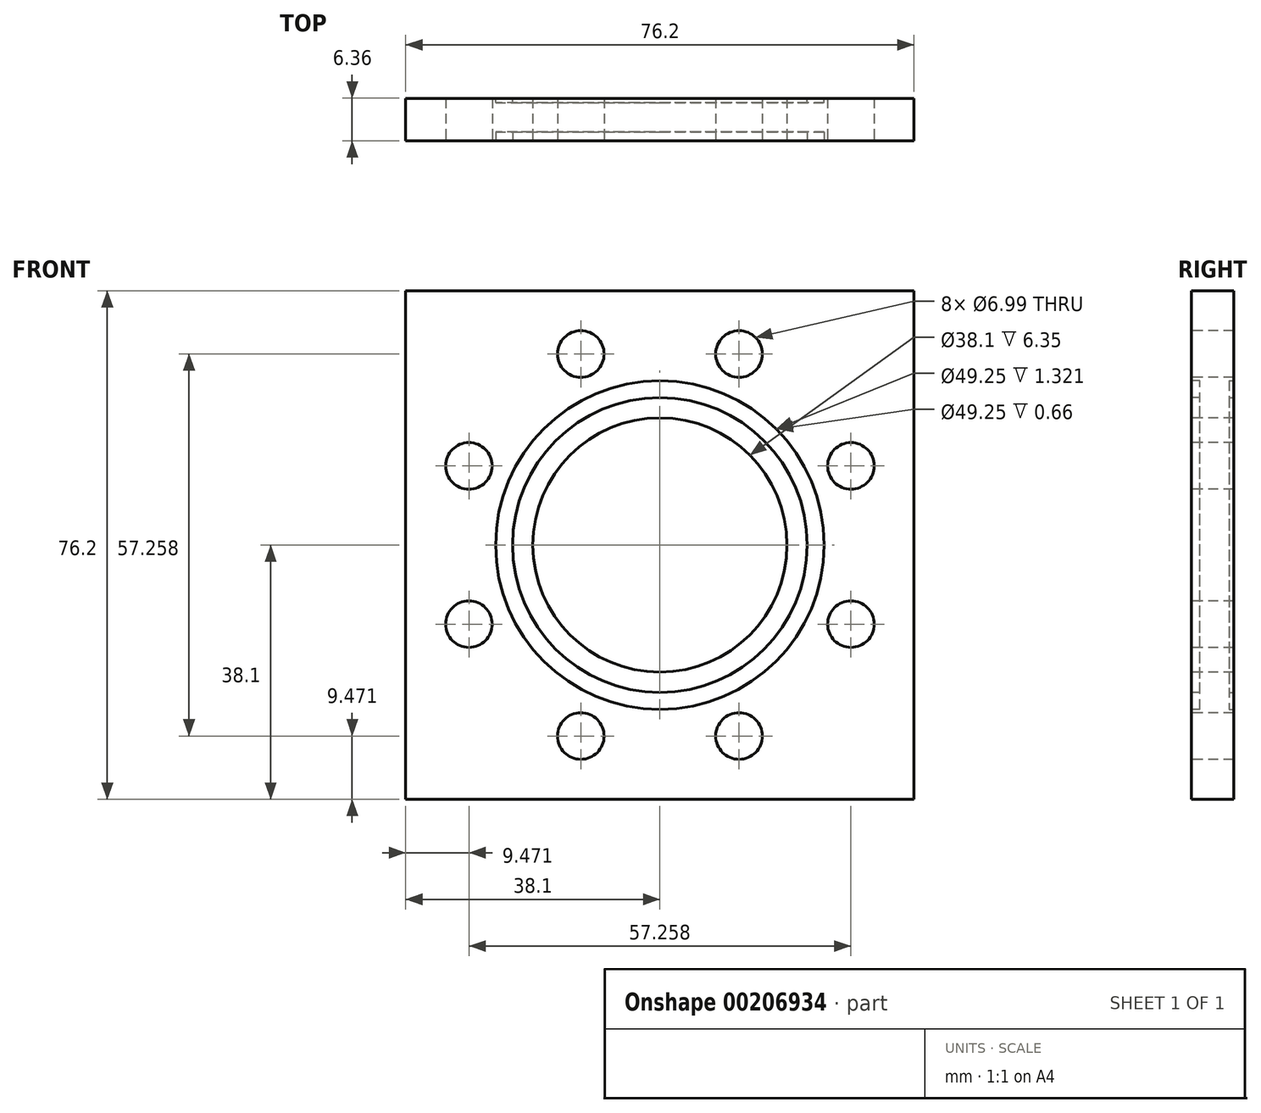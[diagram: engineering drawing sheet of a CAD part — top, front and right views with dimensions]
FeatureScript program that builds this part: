
annotation { "Feature Type Name" : "Feature", "Feature Type Description" : "" }
export const myFeature = defineFeature(function(context is Context, id is Id, definition is map)
    precondition{}
    {
        {
            var Q0;
            Q0=qCreatedBy(makeId("Front.planeOp"),FACE);
            var sketch = newSketch(context, id + "F0", { "sketchPlane" : qUnion([Q0])});
            skLineSegment(sketch, "E0.bottom", {"start": v(-38.1, 38.1) * mm, "end": v(38.1, 38.1) * mm});
            skLineSegment(sketch, "E0.top", {"start": v(-38.1, -38.1) * mm, "end": v(38.1, -38.1) * mm});
            skLineSegment(sketch, "E0.left", {"start": v(-38.1, 38.1) * mm, "end": v(-38.1, -38.1) * mm});
            skLineSegment(sketch, "E0.right", {"start": v(38.1, 38.1) * mm, "end": v(38.1, -38.1) * mm});
            skSolve(sketch);
        }
        {
            var Q0;
            Q0=qSketchRegion(id+"F0",true);
            extrude(context, id + "F1", {"entities" : qUnion([Q0]), "endBound" : BoundingType.SYMMETRIC, "depth" : 6.35 * mm});
        }
        {
            var Q0;
            Q0=makeQuery(id+"F1.opExtrude","CAP_FACE",FACE,{"disambiguationData":[OSD([sQuery(id+"F0.wireOp",EDGE,"E0.bottom"),sQuery(id+"F0.wireOp",EDGE,"E0.top"),sQuery(id+"F0.wireOp",EDGE,"E0.left"),sQuery(id+"F0.wireOp",EDGE,"E0.right")])],"isStart":false});
            var sketch = newSketch(context, id + "F2", { "sketchPlane" : qUnion([Q0])});
            skLineSegment(sketch, "E1", {"start": v(0, 0) * mm, "end": v(11.86, 28.63) * mm, "construction": true});
            skCircle(sketch, "E2", {"center": v(11.86, 28.63) * mm, "radius": 3.5 * mm});
            skCircle(sketch, "E3.1.0", {"center": v(-11.86, 28.63) * mm, "radius": 3.5 * mm});
            skCircle(sketch, "E3.2.0", {"center": v(-28.63, 11.86) * mm, "radius": 3.5 * mm});
            skCircle(sketch, "E3.3.0", {"center": v(-28.63, -11.86) * mm, "radius": 3.5 * mm});
            skCircle(sketch, "E3.4.0", {"center": v(-11.86, -28.63) * mm, "radius": 3.5 * mm});
            skCircle(sketch, "E3.5.0", {"center": v(11.86, -28.63) * mm, "radius": 3.5 * mm});
            skCircle(sketch, "E3.6.0", {"center": v(28.63, -11.86) * mm, "radius": 3.5 * mm});
            skCircle(sketch, "E3.7.0", {"center": v(28.63, 11.86) * mm, "radius": 3.5 * mm});
            skPoint(sketch, "E3.center", {"position": v(0, 0) * mm});
            skSolve(sketch);
        }
        {
            var Q0;
            Q0=qSketchRegion(id+"F2",true);
            extrude(context, id + "F3", {"entities" : qUnion([Q0]), "operationType" : NewBodyOperationType.REMOVE, "oppositeDirection" : true, "depth" : 25.4 * mm});
        }
        {
            var Q0;
            Q0=makeQuery(id+"F1.opExtrude","CAP_FACE",FACE,{"disambiguationData":[OSD([sQuery(id+"F0.wireOp",EDGE,"E0.bottom"),sQuery(id+"F0.wireOp",EDGE,"E0.top"),sQuery(id+"F0.wireOp",EDGE,"E0.left"),sQuery(id+"F0.wireOp",EDGE,"E0.right")])],"isStart":false});
            var sketch = newSketch(context, id + "F4", { "sketchPlane" : qUnion([Q0])});
            skCircle(sketch, "E4", {"center": v(0, 0) * mm, "radius": 19.05 * mm});
            skSolve(sketch);
        }
        {
            var Q0;
            Q0=qSketchRegion(id+"F4",true);
            extrude(context, id + "F5", {"entities" : qUnion([Q0]), "operationType" : NewBodyOperationType.REMOVE, "oppositeDirection" : true, "depth" : 25.4 * mm});
        }
        {
            var Q0;
            Q0=makeQuery(id+"F1.opExtrude","CAP_FACE",FACE,{"disambiguationData":[OSD([sQuery(id+"F0.wireOp",EDGE,"E0.bottom"),sQuery(id+"F0.wireOp",EDGE,"E0.top"),sQuery(id+"F0.wireOp",EDGE,"E0.left"),sQuery(id+"F0.wireOp",EDGE,"E0.right")])],"isStart":false});
            var sketch = newSketch(context, id + "F6", { "sketchPlane" : qUnion([Q0])});
            skCircle(sketch, "E5", {"center": v(0, 0) * mm, "radius": 22.09 * mm});
            skCircle(sketch, "E6", {"center": v(0, 0) * mm, "radius": 24.63 * mm});
            skSolve(sketch);
        }
        {
            var Q0;
            Q0 = qSketchRegion(id + "F6", true);
            extrude(context, id + "F7", {"entities" : qUnion([Q0]), "operationType" : NewBodyOperationType.REMOVE, "oppositeDirection" : true, "depth" : 1.32 * mm});
        }
        {
            var Q0;
            Q0=makeQuery(id+"F1.opExtrude","CAP_FACE",FACE,{"disambiguationData":[OSD([sQuery(id+"F0.wireOp",EDGE,"E0.bottom"),sQuery(id+"F0.wireOp",EDGE,"E0.top"),sQuery(id+"F0.wireOp",EDGE,"E0.left"),sQuery(id+"F0.wireOp",EDGE,"E0.right")])],"isStart":true});
            var sketch = newSketch(context, id + "F8", { "sketchPlane" : qUnion([Q0])});
            skCircle(sketch, "E7", {"center": v(0, 0) * mm, "radius": 22.09 * mm});
            skCircle(sketch, "E8", {"center": v(0, 0) * mm, "radius": 24.63 * mm});
            skSolve(sketch);
        }
        {
            var Q0;
            Q0 = qSketchRegion(id + "F8", true);
            extrude(context, id + "F9", {"entities" : qUnion([Q0]), "operationType" : NewBodyOperationType.REMOVE, "oppositeDirection" : true, "depth" : 0.66 * mm});
        }
    });
